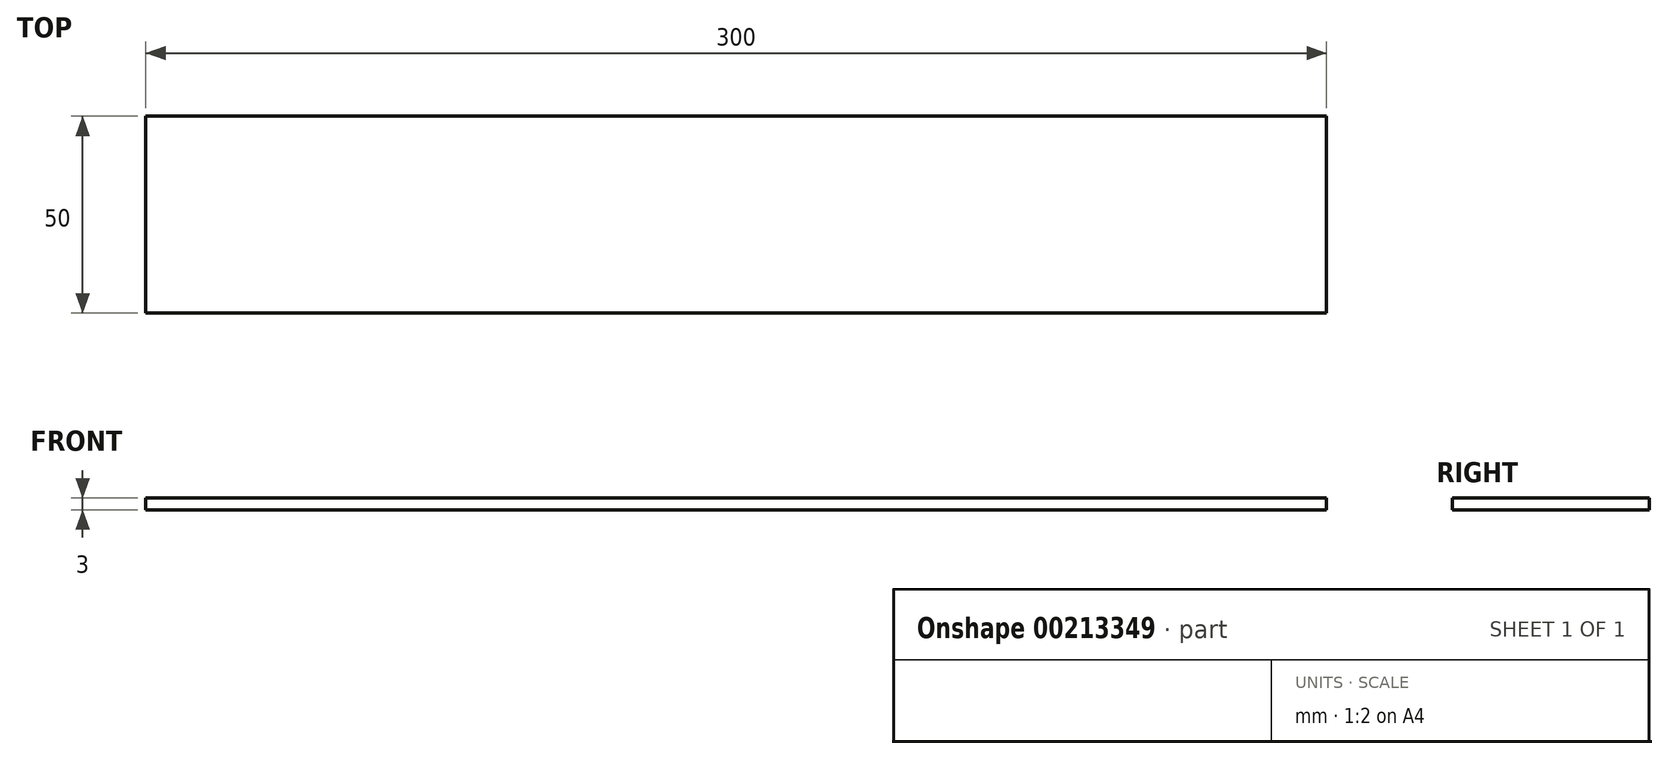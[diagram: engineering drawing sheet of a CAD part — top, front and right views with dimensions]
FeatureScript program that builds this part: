
annotation { "Feature Type Name" : "Feature", "Feature Type Description" : "" }
export const myFeature = defineFeature(function(context is Context, id is Id, definition is map)
    precondition{}
    {
        {
            var Q0;
            Q0=qCreatedBy(makeId("Top.planeOp"),FACE);
            var sketch = newSketch(context, id + "F0", { "sketchPlane" : qUnion([Q0])});
            skLineSegment(sketch, "E0.bottom", {"start": v(150, 25) * mm, "end": v(-150, 25) * mm});
            skLineSegment(sketch, "E0.top", {"start": v(150, -25) * mm, "end": v(-150, -25) * mm});
            skLineSegment(sketch, "E0.left", {"start": v(150, 25) * mm, "end": v(150, -25) * mm});
            skLineSegment(sketch, "E0.right", {"start": v(-150, 25) * mm, "end": v(-150, -25) * mm});
            skPoint(sketch, "E0.middle", {"position": v(0, 0) * mm});
            skLineSegment(sketch, "E1", {"start": v(-150, 25) * mm, "end": v(-79.68, 102.98) * mm});
            skSolve(sketch);
        }
        {
            var Q0;
            Q0=makeQuery(id+"F0.imprint","IMPRINT",FACE,{"disambiguationData":[TD([[makeQuery(id+"F0.imprint","IMPRINT",EDGE,{"derivedFrom":sQuery(id+"F0.wireOp",EDGE,"E0.bottom")}),1.0]])]});
            extrude(context, id + "F1", {"entities" : qUnion([Q0]), "depth" : 3 * mm});
        }
    });
